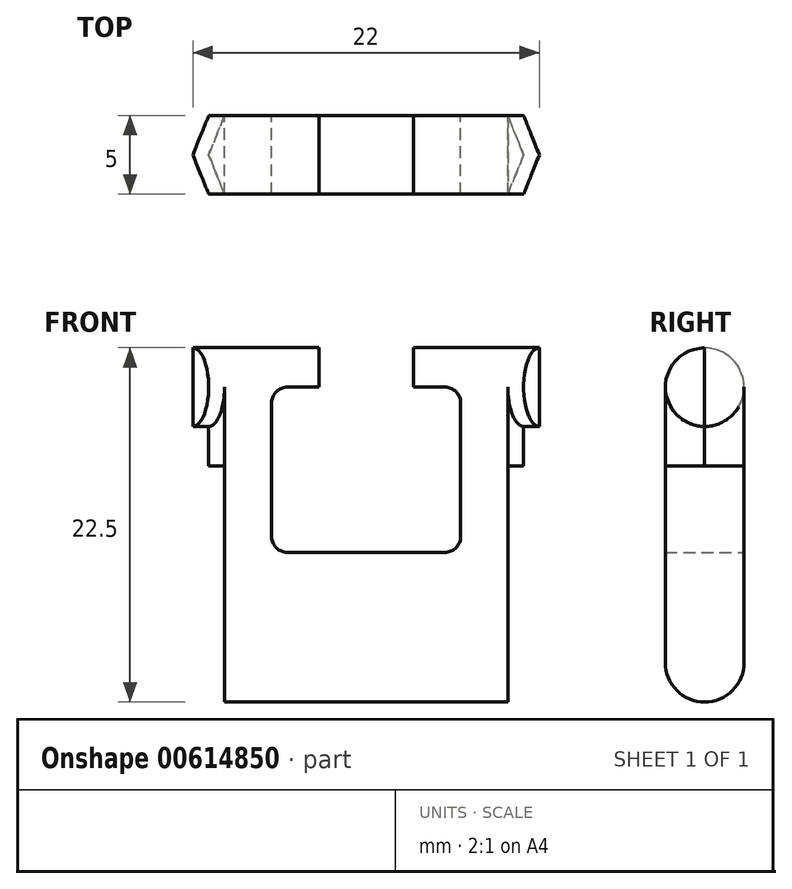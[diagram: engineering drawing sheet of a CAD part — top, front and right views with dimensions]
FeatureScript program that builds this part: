
annotation { "Feature Type Name" : "Feature", "Feature Type Description" : "" }
export const myFeature = defineFeature(function(context is Context, id is Id, definition is map)
    precondition{}
    {
        {
            var Q0;
            Q0=qCreatedBy(makeId("Front.planeOp"),FACE);
            var sketch = newSketch(context, id + "F0", { "sketchPlane" : qUnion([Q0])});
            skLineSegment(sketch, "E0", {"start": v(0, 0) * mm, "end": v(9, 0) * mm});
            skLineSegment(sketch, "E1", {"start": v(9, 0) * mm, "end": v(9, 14) * mm});
            skLineSegment(sketch, "E2", {"start": v(9, 14) * mm, "end": v(6, 14) * mm});
            skLineSegment(sketch, "E3", {"start": v(6, 14) * mm, "end": v(6, 3.5) * mm});
            skLineSegment(sketch, "E4", {"start": v(6, 3.5) * mm, "end": v(0, 3.5) * mm});
            skLineSegment(sketch, "E5", {"start": v(0, 3.5) * mm, "end": v(0, 0) * mm});
            skSolve(sketch);
        }
        {
            var Q0;
            Q0=qCreatedBy(makeId("Right.planeOp"),FACE);
            var sketch = newSketch(context, id + "F1", { "sketchPlane" : qUnion([Q0])});
            skCircle(sketch, "E6", {"center": v(0, 14) * mm, "radius": 2.5 * mm});
            skLineSegment(sketch, "E7", {"start": v(-2.5, 14) * mm, "end": v(2.5, 14) * mm});
            skSolve(sketch);
        }
        {
            var Q0;
            Q0 = qSketchRegion(id + "F0", true);
            extrude(context, id + "F2", {"entities" : qUnion([Q0]), "endBound" : BoundingType.SYMMETRIC, "depth" : 5 * mm, "offsetDistance" : 25 * mm});
        }
        {
            var Q0;
            Q0 = qSketchRegion(id + "F1", true);
            extrude(context, id + "F3", {"entities" : qUnion([Q0]), "operationType" : NewBodyOperationType.ADD, "depth" : 10 * mm, "offsetDistance" : 25 * mm});
        }
        {
            var Q0;
            Q0 = qSketchRegion(id + "F1", true);
            extrude(context, id + "F4", {"entities" : qUnion([Q0]), "operationType" : NewBodyOperationType.REMOVE, "depth" : 3 * mm, "offsetDistance" : 25 * mm});
        }
        {
            var Q0;
            {var subQ0=sQuery(id+"F1.wireOp",EDGE,"E7");Q0=makeQuery(id+"F1.imprint","IMPRINT",FACE,{"disambiguationData":[TD([[makeQuery(id+"F1.imprint","IMPRINT",EDGE,{"derivedFrom":subQ0}),-1.0]])]});}
            extrude(context, id + "F5", {"entities" : qUnion([Q0]), "operationType" : NewBodyOperationType.REMOVE, "depth" : 6 * mm, "offsetDistance" : 25 * mm});
        }
        {
            var Q0;
            Q0=makeQuery(id+"F5.boolean.opBoolean","COPY",EDGE,{"derivedFrom":makeQuery(id+"F5.opExtrude","CAP_EDGE",EDGE,{"disambiguationData":[OSD([sQuery(id+"F1.wireOp",EDGE,"E7")])],"isStart":false})});
            var Q1;
            Q1=makeQuery(id+"F2.opExtrude","SWEPT_EDGE",EDGE,{"disambiguationData":[OSD([sQuery(id+"F0.wireOp",EDGE,"E3"),sQuery(id+"F0.wireOp",EDGE,"E4")])]});
            fillet(context, id + "F6", {"entities" : qUnion([Q0, Q1]), "radius" : 1 * mm, "tangentPropagation" : true, "allowEdgeOverflow" : false});
        }
        {
            var Q0;
            Q0=qCreatedBy(makeId("Top.planeOp"),FACE);
            var sketch = newSketch(context, id + "F7", { "sketchPlane" : qUnion([Q0])});
            skLineSegment(sketch, "E8", {"start": v(9, -2.5) * mm, "end": v(10, 0) * mm});
            skLineSegment(sketch, "E9", {"start": v(9, 2.5) * mm, "end": v(10, 0) * mm});
            skLineSegment(sketch, "E10", {"start": v(9, -2.5) * mm, "end": v(9, 2.5) * mm});
            skLineSegment(sketch, "E11", {"start": v(10, -2.5) * mm, "end": v(11, 0) * mm});
            skLineSegment(sketch, "E12", {"start": v(10, 2.5) * mm, "end": v(11, 0) * mm});
            skLineSegment(sketch, "E13", {"start": v(10, -2.5) * mm, "end": v(11.5, -2.5) * mm});
            skLineSegment(sketch, "E14", {"start": v(11.5, -2.5) * mm, "end": v(11.5, 2.5) * mm});
            skLineSegment(sketch, "E15", {"start": v(11.5, 2.5) * mm, "end": v(10, 2.5) * mm});
            skSolve(sketch);
        }
        {
            var Q0;
            Q0=makeQuery(id+"F7.imprint","IMPRINT",FACE,{"disambiguationData":[TD([[makeQuery(id+"F7.imprint","IMPRINT",EDGE,{"derivedFrom":sQuery(id+"F7.wireOp",EDGE,"E8")}),1.0]])]});
            extrude(context, id + "F8", {"entities" : qUnion([Q0]), "operationType" : NewBodyOperationType.ADD, "depth" : 14 * mm, "offsetDistance" : 25 * mm});
        }
        {
            var Q0;
            Q0=makeQuery(id+"F7.imprint","IMPRINT",FACE,{"disambiguationData":[TD([[makeQuery(id+"F7.imprint","IMPRINT",EDGE,{"derivedFrom":sQuery(id+"F7.wireOp",EDGE,"E8")}),1.0]])]});
            extrude(context, id + "F9", {"entities" : qUnion([Q0]), "operationType" : NewBodyOperationType.REMOVE, "depth" : 9 * mm, "offsetDistance" : 25 * mm});
        }
        {
            var Q0;
            Q0=makeQuery(id+"F3.opExtrude","CAP_FACE",FACE,{"disambiguationData":[OSD([sQuery(id+"F1.wireOp",EDGE,"E6")])],"isStart":false});
            extrude(context, id + "F10", {"entities" : qUnion([Q0]), "operationType" : NewBodyOperationType.ADD, "depth" : 1 * mm, "offsetDistance" : 25 * mm});
        }
        {
            var Q0;
            Q0=makeQuery(id+"F7.imprint","IMPRINT",FACE,{"disambiguationData":[TD([[makeQuery(id+"F7.imprint","IMPRINT",EDGE,{"derivedFrom":sQuery(id+"F7.wireOp",EDGE,"E11")}),-1.0]])]});
            extrude(context, id + "F11", {"entities" : qUnion([Q0]), "operationType" : NewBodyOperationType.REMOVE, "depth" : 16.5 * mm, "offsetDistance" : 25 * mm});
        }
        {
            var Q0;
            Q0=makeQuery(id+"F2.opExtrude","SWEPT_BODY",BODY,{"disambiguationData":[OSD([sQuery(id+"F0.wireOp",EDGE,"E0"),sQuery(id+"F0.wireOp",EDGE,"E1"),sQuery(id+"F0.wireOp",EDGE,"E2"),sQuery(id+"F0.wireOp",EDGE,"E3"),sQuery(id+"F0.wireOp",EDGE,"E4"),sQuery(id+"F0.wireOp",EDGE,"E5")])]});
            var Q1;
            Q1=makeQuery(id+"F2.opExtrude","SWEPT_FACE",FACE,{"disambiguationData":[OSD([sQuery(id+"F0.wireOp",EDGE,"E5")])]});
            mirror(context, id + "F12", {"operationType" : NewBodyOperationType.ADD, "entities" : qUnion([Q0]), "mirrorPlane" : qUnion([Q1])});
        }
        {
            var Q0;
            {var subQ0=makeQuery(id+"F8.boolean.opBoolean","MERGE",FACE,{"derivedFrom":[makeQuery(id+"F2.opExtrude","SWEPT_FACE",FACE,{"disambiguationData":[OSD([sQuery(id+"F0.wireOp",EDGE,"E0")])]}),makeQuery(id+"F8.opExtrude","CAP_FACE",FACE,{"disambiguationData":[OSD([sQuery(id+"F7.wireOp",EDGE,"E8"),sQuery(id+"F7.wireOp",EDGE,"E9"),sQuery(id+"F7.wireOp",EDGE,"E10")])],"isStart":true})]});Q0=makeQuery(id+"F12.boolean.opBoolean","MERGE",FACE,{"derivedFrom":[subQ0,makeQuery(id+"F12.opPattern","COPY",FACE,{"derivedFrom":subQ0,"instanceName":"1"})]});}
            extrude(context, id + "F13", {"entities" : qUnion([Q0]), "operationType" : NewBodyOperationType.ADD, "depth" : 6 * mm, "offsetDistance" : 25 * mm});
        }
        {
            var Q0;
            {var subQ0=sQuery(id+"F0.wireOp",EDGE,"E0");var subQ1=makeQuery(id+"F2.opExtrude","CAP_EDGE",EDGE,{"disambiguationData":[OSD([subQ0])],"isStart":false});Q0=makeQuery(id+"F13.opExtrude","CAP_EDGE",EDGE,{"disambiguationData":[OSD([subQ0]),TDD([makeQuery(id+"F12.boolean.opBoolean","MERGE",EDGE,{"derivedFrom":[subQ1,makeQuery(id+"F12.opPattern","COPY",EDGE,{"derivedFrom":subQ1,"instanceName":"1"})]})])],"isStart":false});}
            var Q1;
            {var subQ0=sQuery(id+"F0.wireOp",EDGE,"E0");var subQ1=makeQuery(id+"F2.opExtrude","CAP_EDGE",EDGE,{"disambiguationData":[OSD([subQ0])],"isStart":true});Q1=makeQuery(id+"F13.opExtrude","CAP_EDGE",EDGE,{"disambiguationData":[OSD([subQ0]),TDD([makeQuery(id+"F12.boolean.opBoolean","MERGE",EDGE,{"derivedFrom":[subQ1,makeQuery(id+"F12.opPattern","COPY",EDGE,{"derivedFrom":subQ1,"instanceName":"1"})]})])],"isStart":false});}
            fillet(context, id + "F14", {"entities" : qUnion([Q0, Q1]), "radius" : 2.5 * mm, "tangentPropagation" : true, "allowEdgeOverflow" : false});
        }
    });
